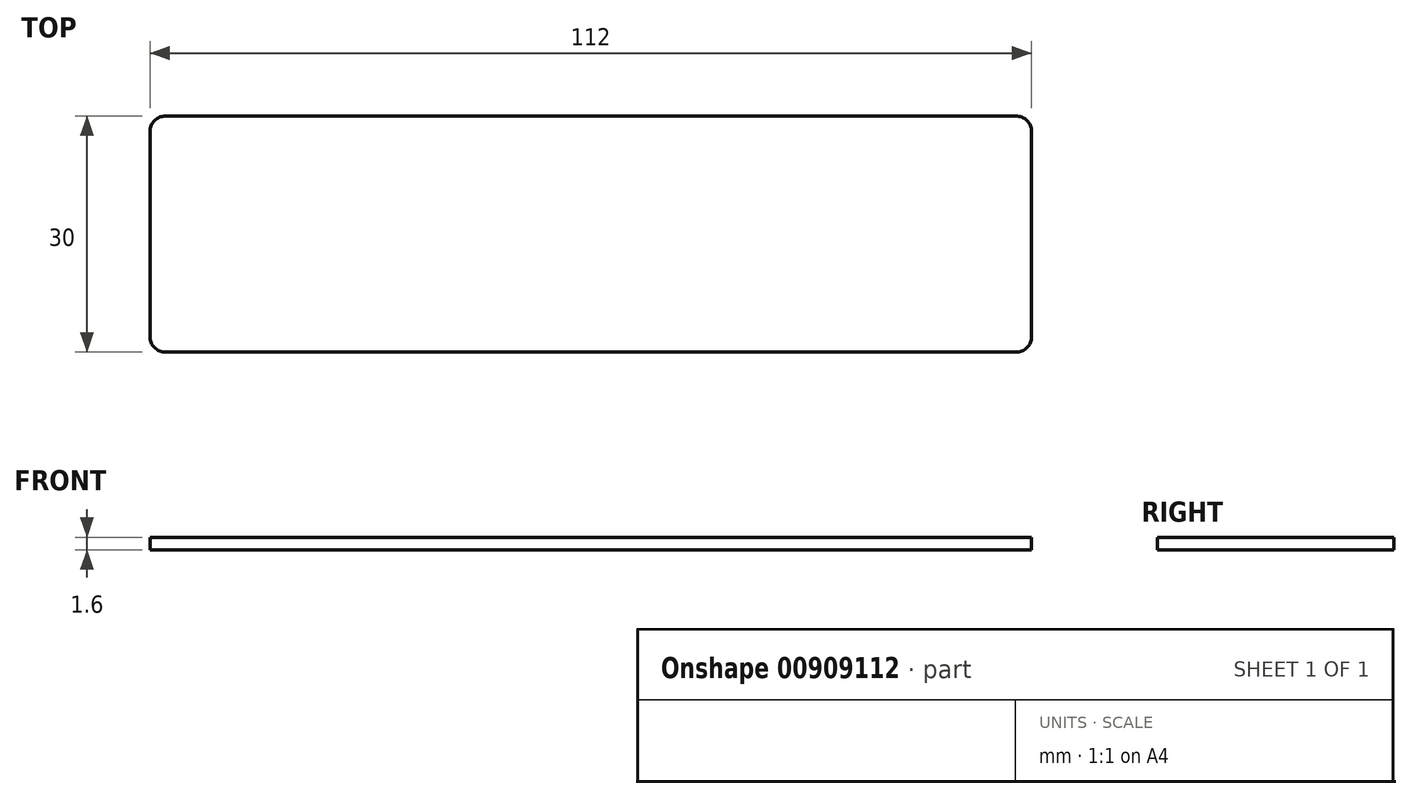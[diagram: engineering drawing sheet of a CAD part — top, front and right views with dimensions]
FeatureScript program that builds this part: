
annotation { "Feature Type Name" : "Feature", "Feature Type Description" : "" }
export const myFeature = defineFeature(function(context is Context, id is Id, definition is map)
    precondition{}
    {
        {
            var Q0;
            Q0=qCreatedBy(makeId("Top.planeOp"),FACE);
            var sketch = newSketch(context, id + "F0", { "sketchPlane" : qUnion([Q0])});
            skLineSegment(sketch, "E0.bottom", {"start": v(56, 15) * mm, "end": v(-56, 15) * mm});
            skLineSegment(sketch, "E0.top", {"start": v(56, -15) * mm, "end": v(-56, -15) * mm});
            skLineSegment(sketch, "E0.left", {"start": v(56, 15) * mm, "end": v(56, -15) * mm});
            skLineSegment(sketch, "E0.right", {"start": v(-56, 15) * mm, "end": v(-56, -15) * mm});
            skPoint(sketch, "E0.middle", {"position": v(0, 0) * mm});
            skSolve(sketch);
        }
        {
            var Q0;
            Q0 = qSketchRegion(id + "F0", true);
            extrude(context, id + "F1", {"entities" : qUnion([Q0]), "flatOperationType" : FlatOperationType.REMOVE, "depth" : 1.6 * mm, "offsetDistance" : 25 * mm, "domain" : OperationDomain.MODEL});
        }
        {
            var Q0;
            Q0=makeQuery(id+"F1.opExtrude","SWEPT_EDGE",EDGE,{"disambiguationData":[OSD([sQuery(id+"F0.wireOp",EDGE,"E0.top"),sQuery(id+"F0.wireOp",EDGE,"E0.right")])]});
            var Q1;
            Q1=makeQuery(id+"F1.opExtrude","SWEPT_EDGE",EDGE,{"disambiguationData":[OSD([sQuery(id+"F0.wireOp",EDGE,"E0.top"),sQuery(id+"F0.wireOp",EDGE,"E0.left")])]});
            var Q2;
            Q2=makeQuery(id+"F1.opExtrude","SWEPT_EDGE",EDGE,{"disambiguationData":[OSD([sQuery(id+"F0.wireOp",EDGE,"E0.bottom"),sQuery(id+"F0.wireOp",EDGE,"E0.left")])]});
            var Q3;
            Q3=makeQuery(id+"F1.opExtrude","SWEPT_EDGE",EDGE,{"disambiguationData":[OSD([sQuery(id+"F0.wireOp",EDGE,"E0.bottom"),sQuery(id+"F0.wireOp",EDGE,"E0.right")])]});
            fillet(context, id + "F2", {"entities" : qUnion([Q0, Q1, Q2, Q3]), "radius" : 2 * mm, "tangentPropagation" : true, "allowEdgeOverflow" : false});
        }
    });
